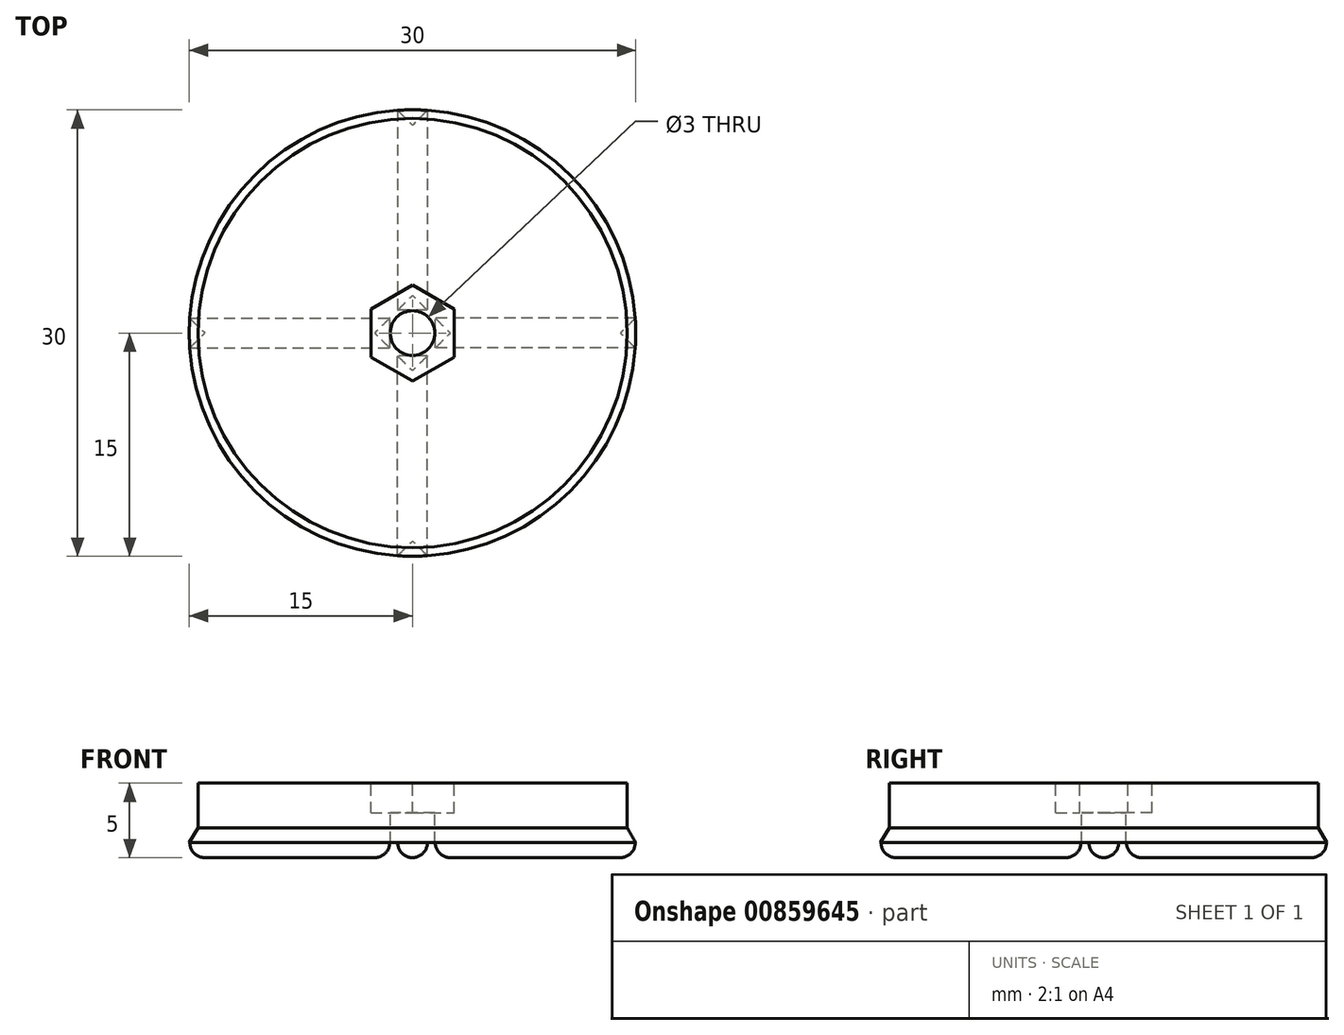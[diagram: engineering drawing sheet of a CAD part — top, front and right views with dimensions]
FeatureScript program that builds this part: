
annotation { "Feature Type Name" : "Feature", "Feature Type Description" : "" }
export const myFeature = defineFeature(function(context is Context, id is Id, definition is map)
    precondition{}
    {
        {
            var Q0;
            Q0=qCreatedBy(makeId("Top.planeOp"),FACE);
            var sketch = newSketch(context, id + "F0", { "sketchPlane" : qUnion([Q0])});
            skCircle(sketch, "E0", {"center": v(0, 0) * mm, "radius": 15 * mm});
            skSolve(sketch);
        }
        {
            var Q0;
            Q0=makeQuery(id+"F0.imprint","IMPRINT",FACE,{"disambiguationData":[TD([[makeQuery(id+"F0.imprint","IMPRINT",EDGE,{"derivedFrom":sQuery(id+"F0.wireOp",EDGE,"E0")}),1.0]])]});
            extrude(context, id + "F1", {"entities" : qUnion([Q0]), "depth" : 1 * mm, "offsetDistance" : 25 * mm, "hasDraft" : true, "draftAngle" : 30 * degree, "draftPullDirection" : true});
        }
        {
            var Q0;
            Q0=makeQuery(id+"F1.opExtrude","CAP_FACE",FACE,{"disambiguationData":[OSD([sQuery(id+"F0.wireOp",EDGE,"E0")])],"isStart":false});
            extrude(context, id + "F2", {"entities" : qUnion([Q0]), "operationType" : NewBodyOperationType.ADD, "depth" : 3 * mm, "offsetDistance" : 25 * mm});
        }
        {
            var Q0;
            Q0=makeQuery(id+"F2.opExtrude","CAP_FACE",FACE,{"disambiguationData":[OSD([sQuery(id+"F0.wireOp",EDGE,"E0")])],"isStart":false});
            var sketch = newSketch(context, id + "F3", { "sketchPlane" : qUnion([Q0])});
            skCircle(sketch, "E1.cCircle", {"center": v(0, 0) * mm, "radius": 2.8 * mm, "construction": true});
            skLineSegment(sketch, "E1.0", {"start": v(2.8, 1.62) * mm, "end": v(2.8, -1.62) * mm});
            skLineSegment(sketch, "E1.1", {"start": v(2.8, -1.62) * mm, "end": v(0, -3.23) * mm});
            skLineSegment(sketch, "E1.2", {"start": v(0, -3.23) * mm, "end": v(-2.8, -1.62) * mm});
            skLineSegment(sketch, "E1.3", {"start": v(-2.8, -1.62) * mm, "end": v(-2.8, 1.62) * mm});
            skLineSegment(sketch, "E1.4", {"start": v(-2.8, 1.62) * mm, "end": v(0, 3.23) * mm});
            skLineSegment(sketch, "E1.5", {"start": v(0, 3.23) * mm, "end": v(2.8, 1.62) * mm});
            skPoint(sketch, "E1.0.midPoint", {"position": v(2.8, 0) * mm});
            skSolve(sketch);
        }
        {
            var Q0;
            Q0=makeQuery(id+"F3.imprint","IMPRINT",FACE,{"disambiguationData":[TD([[makeQuery(id+"F3.imprint","IMPRINT",EDGE,{"derivedFrom":sQuery(id+"F3.wireOp",EDGE,"E1.0")}),-1.0]])]});
            extrude(context, id + "F4", {"entities" : qUnion([Q0]), "operationType" : NewBodyOperationType.REMOVE, "oppositeDirection" : true, "depth" : 2 * mm, "offsetDistance" : 25 * mm});
        }
        {
            var Q0;
            Q0=makeQuery(id+"F4.boolean.opBoolean","COPY",FACE,{"derivedFrom":makeQuery(id+"F4.opExtrude","CAP_FACE",FACE,{"disambiguationData":[OSD([sQuery(id+"F3.wireOp",EDGE,"E1.0"),sQuery(id+"F3.wireOp",EDGE,"E1.1"),sQuery(id+"F3.wireOp",EDGE,"E1.2"),sQuery(id+"F3.wireOp",EDGE,"E1.3"),sQuery(id+"F3.wireOp",EDGE,"E1.4"),sQuery(id+"F3.wireOp",EDGE,"E1.5")])],"isStart":false})});
            var sketch = newSketch(context, id + "F5", { "sketchPlane" : qUnion([Q0])});
            skCircle(sketch, "E2", {"center": v(0, 0) * mm, "radius": 1.5 * mm});
            skSolve(sketch);
        }
        {
            var Q0;
            Q0=makeQuery(id+"F5.imprint","IMPRINT",FACE,{"disambiguationData":[TD([[makeQuery(id+"F5.imprint","IMPRINT",EDGE,{"derivedFrom":sQuery(id+"F5.wireOp",EDGE,"E2")}),1.0]])]});
            extrude(context, id + "F6", {"entities" : qUnion([Q0]), "operationType" : NewBodyOperationType.REMOVE, "endBound" : BoundingType.THROUGH_ALL, "oppositeDirection" : true, "depth" : 25 * mm, "offsetDistance" : 25 * mm});
        }
        {
            var Q0;
            Q0=makeQuery(id+"F1.opExtrude","CAP_FACE",FACE,{"disambiguationData":[OSD([sQuery(id+"F0.wireOp",EDGE,"E0")])],"isStart":true});
            var sketch = newSketch(context, id + "F7", { "sketchPlane" : qUnion([Q0])});
            skLineSegment(sketch, "E3", {"start": v(-1.5, 0) * mm, "end": v(-15, 0) * mm, "construction": true});
            skLineSegment(sketch, "E4", {"start": v(0, 1.5) * mm, "end": v(0, 15) * mm, "construction": true});
            skLineSegment(sketch, "E5", {"start": v(1.5, 0) * mm, "end": v(15, 0) * mm, "construction": true});
            skLineSegment(sketch, "E6", {"start": v(0, -15) * mm, "end": v(0, -1.5) * mm, "construction": true});
            skLineSegment(sketch, "E7.bottom", {"start": v(1, 14.97) * mm, "end": v(-1, 14.97) * mm});
            skLineSegment(sketch, "E7.top", {"start": v(1, 1.53) * mm, "end": v(-1, 1.53) * mm});
            skLineSegment(sketch, "E7.left", {"start": v(1, 14.97) * mm, "end": v(1, 1.53) * mm});
            skLineSegment(sketch, "E7.right", {"start": v(-1, 14.97) * mm, "end": v(-1, 1.53) * mm});
            skPoint(sketch, "E7.middle", {"position": v(0, 8.25) * mm});
            skLineSegment(sketch, "E8.bottom", {"start": v(14.97, 1) * mm, "end": v(1.53, 1) * mm});
            skLineSegment(sketch, "E8.top", {"start": v(14.97, -1) * mm, "end": v(1.53, -1) * mm});
            skLineSegment(sketch, "E8.left", {"start": v(14.97, 1) * mm, "end": v(14.97, -1) * mm});
            skLineSegment(sketch, "E8.right", {"start": v(1.53, 1) * mm, "end": v(1.53, -1) * mm});
            skPoint(sketch, "E8.middle", {"position": v(8.25, 0) * mm});
            skLineSegment(sketch, "E9.MirrorCS", {"start": v(0, 17) * mm, "end": v(0, 3.5) * mm, "construction": true});
            skLineSegment(sketch, "E10.MirrorCS", {"start": v(-14.97, 1) * mm, "end": v(-1.53, 1) * mm});
            skLineSegment(sketch, "E11.MirrorCS", {"start": v(-14.97, -1) * mm, "end": v(-1.53, -1) * mm});
            skLineSegment(sketch, "E12.MirrorCS", {"start": v(-1.53, 1) * mm, "end": v(-1.53, -1) * mm});
            skLineSegment(sketch, "E13.MirrorCS", {"start": v(-14.97, 1) * mm, "end": v(-14.97, -1) * mm});
            skLineSegment(sketch, "E14.MirrorCS", {"start": v(1, -14.97) * mm, "end": v(1, -1.53) * mm});
            skLineSegment(sketch, "E15.MirrorCS", {"start": v(1, -1.53) * mm, "end": v(-1, -1.53) * mm});
            skLineSegment(sketch, "E16.MirrorCS", {"start": v(-1, -14.97) * mm, "end": v(-1, -1.53) * mm});
            skLineSegment(sketch, "E17.MirrorCS", {"start": v(1, -14.97) * mm, "end": v(-1, -14.97) * mm});
            skSolve(sketch);
        }
        {
            var Q0;
            Q0=makeQuery(id+"F7.imprint","IMPRINT",FACE,{"disambiguationData":[TD([[makeQuery(id+"F7.imprint","IMPRINT",EDGE,{"derivedFrom":sQuery(id+"F7.wireOp",EDGE,"E10.MirrorCS")}),-1.0]])]});
            var Q1;
            Q1=makeQuery(id+"F7.imprint","IMPRINT",FACE,{"disambiguationData":[TD([[makeQuery(id+"F7.imprint","IMPRINT",EDGE,{"derivedFrom":sQuery(id+"F7.wireOp",EDGE,"E7.bottom")}),1.0]])]});
            var Q2;
            Q2=makeQuery(id+"F7.imprint","IMPRINT",FACE,{"disambiguationData":[TD([[makeQuery(id+"F7.imprint","IMPRINT",EDGE,{"derivedFrom":sQuery(id+"F7.wireOp",EDGE,"E8.bottom")}),1.0]])]});
            var Q3;
            Q3=makeQuery(id+"F7.imprint","IMPRINT",FACE,{"disambiguationData":[TD([[makeQuery(id+"F7.imprint","IMPRINT",EDGE,{"derivedFrom":sQuery(id+"F7.wireOp",EDGE,"E14.MirrorCS")}),1.0]])]});
            extrude(context, id + "F8", {"entities" : qUnion([Q0, Q1, Q2, Q3]), "operationType" : NewBodyOperationType.ADD, "depth" : 1 * mm, "offsetDistance" : 25 * mm});
        }
        {
            var Q0;
            Q0=makeQuery(id+"F8.opExtrude","CAP_EDGE",EDGE,{"disambiguationData":[OSD([sQuery(id+"F7.wireOp",EDGE,"E16.MirrorCS")])],"isStart":false});
            var Q1;
            Q1=makeQuery(id+"F8.opExtrude","CAP_EDGE",EDGE,{"disambiguationData":[OSD([sQuery(id+"F7.wireOp",EDGE,"E14.MirrorCS")])],"isStart":false});
            var Q2;
            Q2=makeQuery(id+"F8.opExtrude","CAP_EDGE",EDGE,{"disambiguationData":[OSD([sQuery(id+"F7.wireOp",EDGE,"E8.top")])],"isStart":false});
            var Q3;
            Q3=makeQuery(id+"F8.opExtrude","CAP_FACE",FACE,{"disambiguationData":[OSD([sQuery(id+"F7.wireOp",EDGE,"E8.bottom"),sQuery(id+"F7.wireOp",EDGE,"E8.top"),sQuery(id+"F7.wireOp",EDGE,"E8.left"),sQuery(id+"F7.wireOp",EDGE,"E8.right")])],"isStart":false});
            var Q4;
            Q4=makeQuery(id+"F8.opExtrude","CAP_EDGE",EDGE,{"disambiguationData":[OSD([sQuery(id+"F7.wireOp",EDGE,"E11.MirrorCS")])],"isStart":false});
            var Q5;
            Q5=makeQuery(id+"F8.opExtrude","CAP_EDGE",EDGE,{"disambiguationData":[OSD([sQuery(id+"F7.wireOp",EDGE,"E10.MirrorCS")])],"isStart":false});
            var Q6;
            Q6=makeQuery(id+"F8.opExtrude","CAP_EDGE",EDGE,{"disambiguationData":[OSD([sQuery(id+"F7.wireOp",EDGE,"E7.left")])],"isStart":false});
            var Q7;
            Q7=makeQuery(id+"F8.opExtrude","CAP_EDGE",EDGE,{"disambiguationData":[OSD([sQuery(id+"F7.wireOp",EDGE,"E7.right")])],"isStart":false});
            var Q8;
            Q8=makeQuery(id+"F8.opExtrude","CAP_EDGE",EDGE,{"disambiguationData":[OSD([sQuery(id+"F7.wireOp",EDGE,"E17.MirrorCS")])],"isStart":false});
            var Q9;
            Q9=makeQuery(id+"F8.opExtrude","CAP_EDGE",EDGE,{"disambiguationData":[OSD([sQuery(id+"F7.wireOp",EDGE,"E15.MirrorCS")])],"isStart":false});
            var Q10;
            Q10=makeQuery(id+"F8.opExtrude","CAP_EDGE",EDGE,{"disambiguationData":[OSD([sQuery(id+"F7.wireOp",EDGE,"E7.top")])],"isStart":false});
            var Q11;
            Q11=makeQuery(id+"F8.opExtrude","CAP_EDGE",EDGE,{"disambiguationData":[OSD([sQuery(id+"F7.wireOp",EDGE,"E12.MirrorCS")])],"isStart":false});
            var Q12;
            Q12=makeQuery(id+"F8.opExtrude","CAP_EDGE",EDGE,{"disambiguationData":[OSD([sQuery(id+"F7.wireOp",EDGE,"E13.MirrorCS")])],"isStart":false});
            var Q13;
            Q13=makeQuery(id+"F8.opExtrude","CAP_EDGE",EDGE,{"disambiguationData":[OSD([sQuery(id+"F7.wireOp",EDGE,"E7.bottom")])],"isStart":false});
            fillet(context, id + "F9", {"entities" : qUnion([Q0, Q1, Q2, Q3, Q4, Q5, Q6, Q7, Q8, Q9, Q10, Q11, Q12, Q13]), "radius" : 1 * mm, "tangentPropagation" : true, "allowEdgeOverflow" : false});
        }
    });
